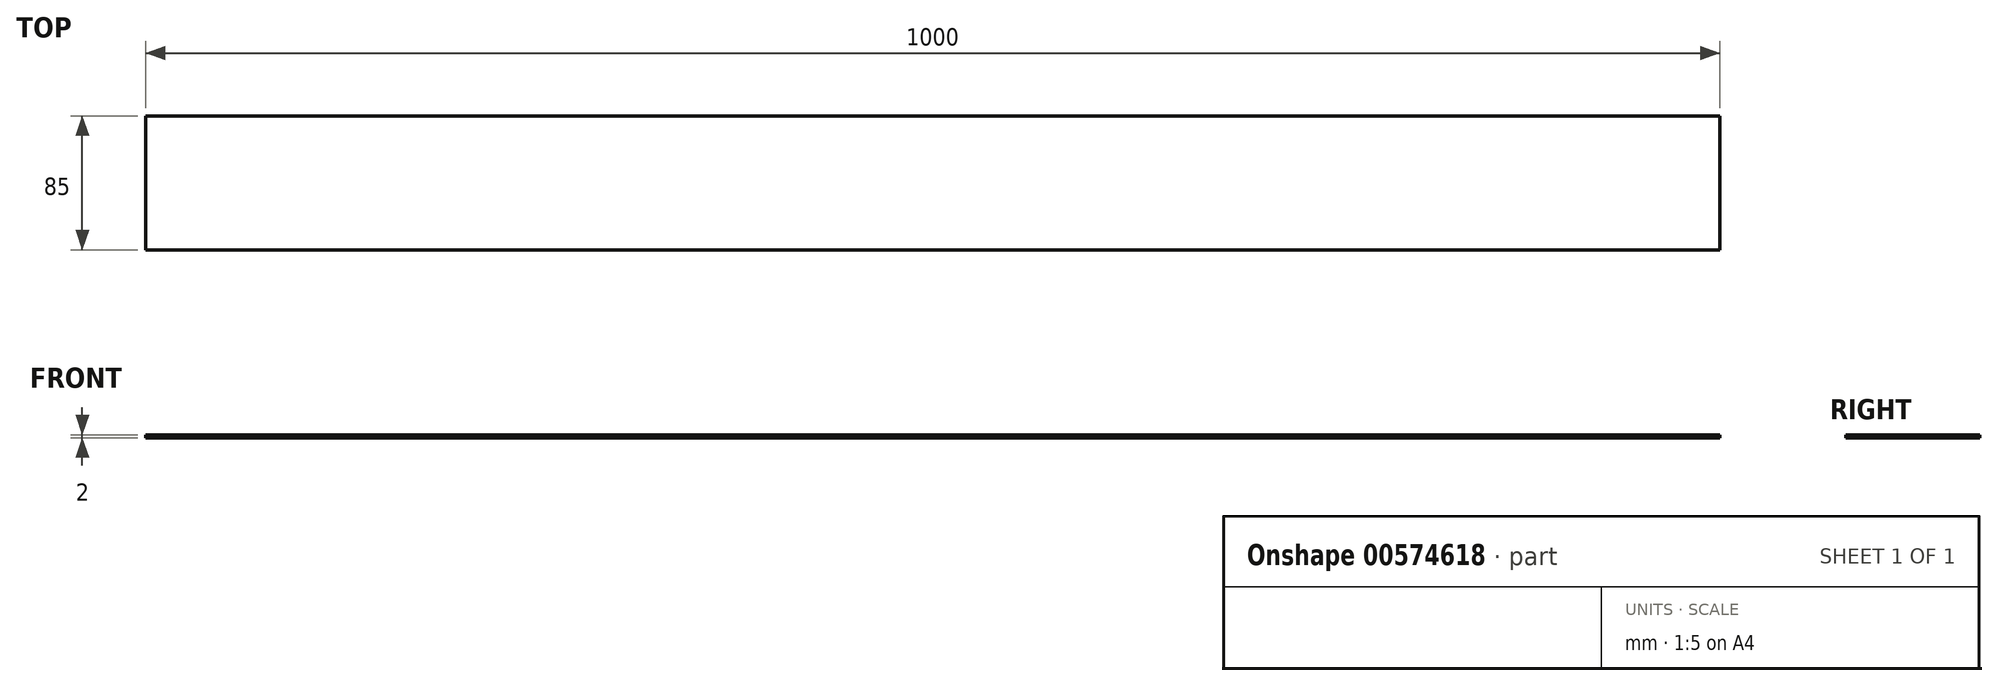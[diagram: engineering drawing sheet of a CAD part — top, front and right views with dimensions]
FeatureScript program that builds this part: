
annotation { "Feature Type Name" : "Feature", "Feature Type Description" : "" }
export const myFeature = defineFeature(function(context is Context, id is Id, definition is map)
    precondition{}
    {
        {
            var Q0;
            Q0=qCreatedBy(makeId("Top.planeOp"),FACE);
            var sketch = newSketch(context, id + "F0", { "sketchPlane" : qUnion([Q0])});
            skLineSegment(sketch, "E0.bottom", {"start": v(0, 0) * mm, "end": v(1000, 0) * mm});
            skLineSegment(sketch, "E0.top", {"start": v(0, 85) * mm, "end": v(1000, 85) * mm});
            skLineSegment(sketch, "E0.left", {"start": v(0, 0) * mm, "end": v(0, 85) * mm});
            skLineSegment(sketch, "E0.right", {"start": v(1000, 0) * mm, "end": v(1000, 85) * mm});
            skSolve(sketch);
        }
        {
            var Q0;
            Q0=makeQuery(id+"F0.imprint","IMPRINT",FACE,{"disambiguationData":[TD([[makeQuery(id+"F0.imprint","IMPRINT",EDGE,{"derivedFrom":sQuery(id+"F0.wireOp",EDGE,"E0.bottom")}),1.0]])]});
            extrude(context, id + "F1", {"entities" : qUnion([Q0]), "depth" : 2 * mm, "offsetDistance" : 25 * mm});
        }
    });
